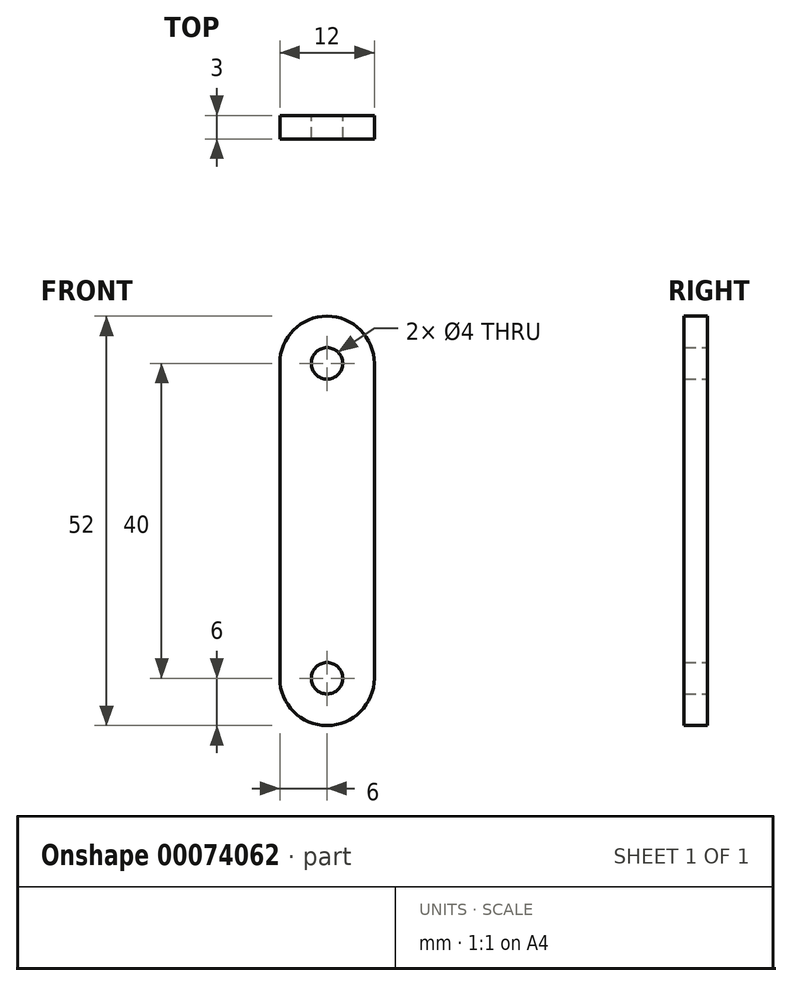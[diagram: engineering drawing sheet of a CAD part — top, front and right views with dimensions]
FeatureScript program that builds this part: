
annotation { "Feature Type Name" : "Feature", "Feature Type Description" : "" }
export const myFeature = defineFeature(function(context is Context, id is Id, definition is map)
    precondition{}
    {
        {
            var Q0;
            Q0=qCreatedBy(makeId("Front.planeOp"),FACE);
            var sketch = newSketch(context, id + "F0", { "sketchPlane" : qUnion([Q0])});
            skCircle(sketch, "E0", {"center": v(0, 0) * mm, "radius": 6 * mm});
            skCircle(sketch, "E1", {"center": v(0, -40) * mm, "radius": 6 * mm});
            skCircle(sketch, "E2", {"center": v(0, 0) * mm, "radius": 2 * mm});
            skCircle(sketch, "E3", {"center": v(0, -40) * mm, "radius": 2 * mm});
            skLineSegment(sketch, "E4", {"start": v(-6, 0) * mm, "end": v(-6, -40) * mm});
            skLineSegment(sketch, "E5", {"start": v(-6, -40) * mm, "end": v(6, -40) * mm});
            skLineSegment(sketch, "E6", {"start": v(6, -40) * mm, "end": v(6, 0) * mm});
            skLineSegment(sketch, "E7", {"start": v(6, 0) * mm, "end": v(-6, 0) * mm});
            skSolve(sketch);
        }
        {
            var Q0;
            Q0=qSketchRegion(id+"F0",true);
            extrude(context, id + "F1", {"entities" : qUnion([Q0]), "depth" : 3 * mm});
        }
    });
